# Revit family: Bottle_Trap-DXV-Modulus-D35700030_Series
name_source: partatom
category: Plumbing Fixtures
revit_build: Autodesk Revit 2018 (Build: 20170223_1515(x64)
units: mm (PartAtom-declared; Revit-internal decimal feet)

## family parameters
Cut with Voids When Loaded = No
Host = Face
OmniClass Number = 23.45.55.21
OmniClass Title = Drains (Wastes)
Part Type = Normal
Room Calculation Point = No
Round Connector Dimension = Use Diameter
Shared = Yes

## types (4) — shared parameters
Assembly Code = D2030
CW Connection = No
Default Elevation = 0"
Description = DXV Modulus Bottle Trap
HW Connection = No
Height = 6 5/16"
IAPMO Compliance = Meets or Exceeds ASME A112.18.1/CSA B125.1,Meets UPC, IPC and NSPC model plumbing codes
Installation Type = Wall Mounted
Length = 13 9/16"
Manufacturer = DXV
Price = Prices may vary. Please consult Manufacturer Representative for most up-to-date price list.
Product Documentation Link = https://dxv01.blob.core.windows.net
Product Page URL = https://www.dxv.com
Revised Date = 04/07/2022
URL = https://www.dxv.com
Vent Connection = No
Waste Connection = Yes
Waste Connection Diameter = 1 1/4"
Width = 3 5/16"
zero-valued in all types: CWFU, HWFU, WFU

## per-type parameters (varying)
| type | Finish | Material |
| D35700030.100 | Brass-DXV-100-Polished Chrome | Brass-DXV-100-Polished Chrome |
| D35700030.144 | Brass-DXV-144-Brushed Nickel | Brass-DXV-144-Brushed Nickel |
| D35700030.150 | Brass-DXV-150-Platinum Nickel | Brass-DXV-150-Platinum Nickel |
| D35700030.243 | Brass-DXV-243-Matte Black | Brass-DXV-243-Matte Black |

note: column(s) folded — value = type name in every type: Model

## geometry (parser evidence)
native form markers: Sweep x3
no freeform markers — native parametric forms only
